# Revit family: LUXI_DOWNLIGHT_OD-E
name_source: partatom
category: Apparecchi per illuminazione
revit_build: Autodesk Revit 2016 (Build: 20161004_0715(x64)
units: mm (PartAtom-declared; Revit-internal decimal feet)

## family parameters
Condiviso = No
Host = Superficie
Numero OmniClass = 23.80.70.00
Punto di calcolo locali = Sì
Quota connettore circolare = Usa diametro
Sorgente d'illuminazione = Sì
Taglio con vuoti quando caricato = No
Tipo di parte = Normale
Titolo OmniClass = Lighting

## types (8) — shared parameters
ANG1 = 50.00°
Alimentatore = Integrato, non dimmerabile
Alimentazione = 220-240V AC / 50-60 Hz
Angolo inclinazione = -90.00°
Certificazioni = CE / RohS
Classe di efficienza energetica = A+
Classe di protezione = II
Classe di rischio fotobiologico = Esente (RG0)
Colore = Bianco
Descrizione = LED Downlight con driver integrato
Fattore di correzione di potenza = ≥0,90 (typ.)
Filtro dei colori = 16777215
Garanzia = 3 anni
Grado di protezione = IP 44 (frontale)
IFCExportAs = IfcLightFixtureType
Indice di resa cromatica = ≥80 (typ.)
Masterformat 2016 Codice = 26.50.00
Masterformat 2016 Descrizione = Lighting
Materiale 1 = Policarbonato_Bianco
Materiale 2 = Tecnopolimero Opalino Diffondente
Modello = Serie OD-E | Downlight
Ottiche = Riflettore metallizzato interno, schermo opalino diffondente
Produttore = Luxi Illuminazione S.r.l.
Prospetto di default = 2000 mm  [stored 6.56168 ft]
Protezione agli urti = IK06 (1 Joule)
Regolazione del flusso luminoso = Non disponibile
Rendi la forma visibile nel rendering = No
Revisione = 3
Sistema di illuminazione = Luce diretta 7 downlight
Sorgente = LED SMD
Spessore Est. = 2 mm  [stored 0.00656168 ft]
Step MacAdam (SDCM) = <4
Temperatura di esercizio = 0°C / +40°C
Tipologie di installazione = Incasso
URL = https://www.luxi.lighting
Uniclass 2015 Codice = EF_70_80
Uniclass 2015 Descrizione = Lighting
Variazione temperatura colore lampada con luminosità attenuata = <Nessuno>
Vita utile = L70B50 30.000ore

## per-type parameters (varying)
| type | Articolo | Carico apparente | Diametro | Dimensioni | Emetti da diametro cerchio | File diagramma fotometrico | H | H_mezzi | H_quarti | Incasso | OFF1 | OFF2 | OFF3 | OFF4 | Peso | Potenza |
| DLDE010100W830 | DLDE010100W830 | 10 VA | 113 mm  [stored 0.370735 ft] | Ø113x59 incasso Ø100 | 100 mm  [stored 0.328084 ft] | DLDE010100W830 Luxi Serie OD-E 10W 3000K.IES | 59 mm | 30 mm | 15 mm | 100 mm  [stored 0.328084 ft] | 25 mm  [stored 0.082021 ft] | 10 mm  [stored 0.0328084 ft] | 7 mm  [stored 0.0229659 ft] | 7 mm  [stored 0.0229659 ft] | 0.30 kg | 10 W |
| DLDE010100W840 | DLDE010100W840 | 10 VA | 113 mm  [stored 0.370735 ft] | Ø113x59 incasso Ø100 | 100 mm  [stored 0.328084 ft] | DLDE010100W840 Luxi Serie OD-E 10W 4000K.IES | 59 mm | 30 mm | 15 mm | 100 mm  [stored 0.328084 ft] | 25 mm  [stored 0.082021 ft] | 10 mm  [stored 0.0328084 ft] | 7 mm  [stored 0.0229659 ft] | 7 mm  [stored 0.0229659 ft] | 0.30 kg | 10 W |
| DLDE017150W830 | DLDE017150W830 | 17 VA | 174 mm  [stored 0.570866 ft] | Ø174x66 incasso Ø150 | 150 mm | DLDE017150W830 Luxi Serie OD-E 17W 3000K.IES | 66 mm  [stored 0.216535 ft] | 33 mm  [stored 0.108268 ft] | 17 mm | 150 mm | 28 mm | 11 mm | 8 mm  [stored 0.0262467 ft] | 12 mm  [stored 0.0393701 ft] | 0.30 kg | 17 W |
| DLDE017150W840 | DLDE017150W830 | 17 VA | 174 mm  [stored 0.570866 ft] | Ø174x66 incasso Ø150 | 150 mm | DLDE017150W840 Luxi Serie OD-E 17W 4000K.IES | 66 mm  [stored 0.216535 ft] | 33 mm  [stored 0.108268 ft] | 17 mm | 150 mm | 28 mm | 11 mm | 8 mm  [stored 0.0262467 ft] | 12 mm  [stored 0.0393701 ft] | 0.30 kg | 17 W |
| DLDE025200W830 | DLDE025200W830 | 25 VA | 224 mm  [stored 0.734908 ft] | Ø224x85 incasso Ø200 | 200 mm  [stored 0.656168 ft] | DLDE025200W830 Luxi Serie OD-E 25W 3000K.IES | 85 mm  [stored 0.278871 ft] | 43 mm | 21 mm | 200 mm  [stored 0.656168 ft] | 36 mm | 14 mm  [stored 0.0459318 ft] | 11 mm | 12 mm  [stored 0.0393701 ft] | 0.50 kg | 25 W |
| DLDE025200W840 | DLDE025200W840 | 25 VA | 224 mm  [stored 0.734908 ft] | Ø224x85 incasso Ø200 | 200 mm  [stored 0.656168 ft] | DLDE025200W840 Luxi Serie OD-E 25W 4000K.IES | 85 mm  [stored 0.278871 ft] | 43 mm | 21 mm | 200 mm  [stored 0.656168 ft] | 36 mm | 14 mm  [stored 0.0459318 ft] | 11 mm | 12 mm  [stored 0.0393701 ft] | 0.50 kg | 25 W |
| DLDE035240W830 | DLDE035240W830 | 35 VA | 279 mm | Ø279x119 incasso Ø240 | 240 mm  [stored 0.787402 ft] | DLDE035240W830 Luxi Serie OD-E 35W 3000K.IES | 119 mm  [stored 0.39042 ft] | 60 mm | 30 mm | 240 mm  [stored 0.787402 ft] | 50 mm  [stored 0.164042 ft] | 20 mm | 15 mm | 20 mm | 0.60 kg | 35 W |
| DLDE035240W840 | DLDE035240W840 | 35 VA | 279 mm | Ø279x119 incasso Ø240 | 240 mm  [stored 0.787402 ft] | DLDE035240W840 Luxi Serie OD-E 35W 4000K.IES | 119 mm  [stored 0.39042 ft] | 60 mm | 30 mm | 240 mm  [stored 0.787402 ft] | 50 mm  [stored 0.164042 ft] | 20 mm | 15 mm | 20 mm | 0.60 kg | 35 W |

note: [stored X ft] marks values corroborated as IEEE doubles in the binary element streams (Revit-internal decimal feet)
